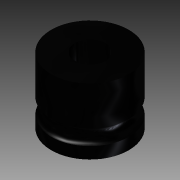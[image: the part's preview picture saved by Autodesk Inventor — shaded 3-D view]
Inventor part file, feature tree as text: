
AUTODESK INVENTOR PART (.ipt)
format: ipt  version: 2013 (Build 170138000, 138)  size: 112,128 bytes
history: native  units: mm
features: revolve x1, sketch x1
ambient origin geometry x8: Origin, YZ Plane, XZ Plane, XY Plane, X Axis, Y Axis, Z Axis, Center Point
bodies: Solid1 (feature_tree)
feature tree (2):
  revolve  "Revolution1"  [1 undecoded]
  sketch  "Sketch1"  dims[d0=2.5mm d1=6.35mm d2=5.3975mm d3=10.795mm d4=7.62mm d5=2.54mm d6=90.0deg]
note: 1 required parameter value undecoded (feature->parameter linkage not recoverable at this tier; creation-order binding heuristic only, values carry confidence <= 0.55)
